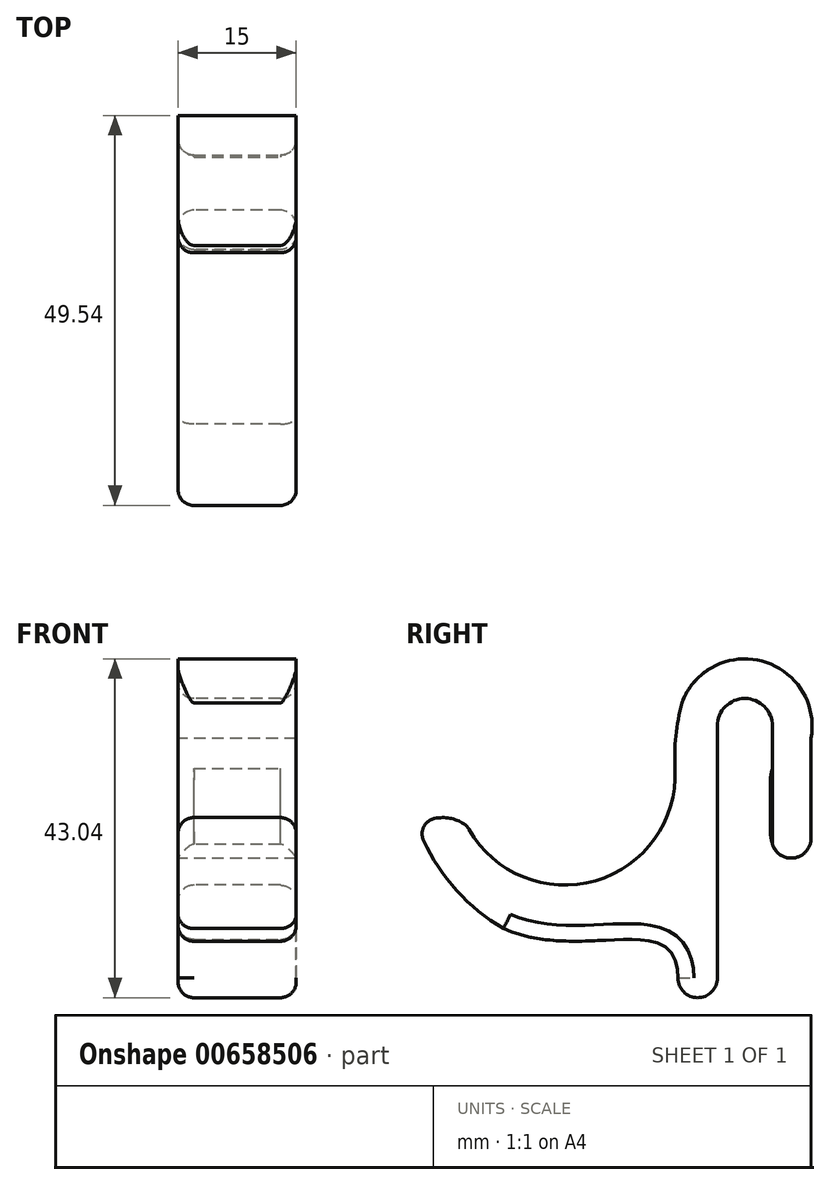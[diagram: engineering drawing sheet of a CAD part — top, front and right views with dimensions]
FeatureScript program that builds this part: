
annotation { "Feature Type Name" : "Feature", "Feature Type Description" : "" }
export const myFeature = defineFeature(function(context is Context, id is Id, definition is map)
    precondition{}
    {
        {
            var Q0;
            Q0=qCreatedBy(makeId("Right.planeOp"),FACE);
            var sketch = newSketch(context, id + "F0", { "sketchPlane" : qUnion([Q0])});
            skLineSegment(sketch, "E0.left", {"start": v(0, 0) * mm, "end": v(0, 32) * mm});
            skLineSegment(sketch, "E0.right", {"start": v(7, 17) * mm, "end": v(7, 32) * mm});
            skArc(sketch, "E1", {"start": v(7, 32) * mm, "mid": v(3.5, 35.5) * mm, "end": v(0, 32) * mm});
            skLineSegment(sketch, "E2.0", {"start": v(11.9, 17.72) * mm, "end": v(11.9, 30.43) * mm});
            skArc(sketch, "E2.1", {"start": v(11.9, 30.43) * mm, "mid": v(5.77, 40.23) * mm, "end": v(-4.5, 34.97) * mm});
            skArc(sketch, "E3", {"start": v(7, 17) * mm, "mid": v(9.76, 15.25) * mm, "end": v(11.9, 17.72) * mm});
            skArc(sketch, "E4", {"start": v(-5, 0) * mm, "mid": v(-2.5, -2.5) * mm, "end": v(0, 0) * mm});
            skLineSegment(sketch, "E5", {"start": v(-4.5, 34.97) * mm, "end": v(-6, 29.97) * mm});
            skArc(sketch, "E6", {"start": v(-31.74, 19.25) * mm, "mid": v(-13.98, 12.87) * mm, "end": v(-6, 29.97) * mm});
            skArc(sketch, "E7", {"start": v(-31.74, 19.25) * mm, "mid": v(-34.9, 20.37) * mm, "end": v(-38.06, 19.25) * mm});
            skArc(sketch, "E8", {"start": v(-38.06, 19.25) * mm, "mid": v(-33.74, 11.83) * mm, "end": v(-27.18, 6.28) * mm});
            skFitSpline(sketch, "E9", {"points": [v(-27.18, 6.28) * mm, v(-5, 0) * mm], "startDerivative": vector(30.25, -13.4) * mm, "endDerivative": vector(-0.02, -27.31) * mm});
            skSolve(sketch);
        }
        {
            var Q0;
            Q0=makeQuery(id+"F0.imprint","IMPRINT",FACE,{"disambiguationData":[TD([[makeQuery(id+"F0.imprint","IMPRINT",EDGE,{"derivedFrom":sQuery(id+"F0.wireOp",EDGE,"E0.left")}),1.0]])]});
            extrude(context, id + "F1", {"entities" : qUnion([Q0]), "depth" : 15 * mm, "offsetDistance" : 25 * mm});
        }
        {
            var Q0;
            Q0=makeQuery(id+"F1.opExtrude","SWEPT_EDGE",EDGE,{"disambiguationData":[OSD([sQuery(id+"F0.wireOp",EDGE,"E5"),sQuery(id+"F0.wireOp",EDGE,"E6")])]});
            fillet(context, id + "F2", {"entities" : qUnion([Q0]), "radius" : 28.53 * mm, "tangentPropagation" : true, "allowEdgeOverflow" : false});
        }
        {
            var Q0;
            Q0=makeQuery(id+"F1.opExtrude","SWEPT_EDGE",EDGE,{"disambiguationData":[OSD([sQuery(id+"F0.wireOp",EDGE,"E6"),sQuery(id+"F0.wireOp",EDGE,"E7")])]});
            var Q1;
            Q1=makeQuery(id+"F1.opExtrude","SWEPT_EDGE",EDGE,{"disambiguationData":[OSD([sQuery(id+"F0.wireOp",EDGE,"E7"),sQuery(id+"F0.wireOp",EDGE,"E8")])]});
            fillet(context, id + "F3", {"entities" : qUnion([Q0, Q1]), "radius" : 2 * mm, "tangentPropagation" : true, "allowEdgeOverflow" : false});
        }
        {
            var Q0;
            Q0=makeQuery(id+"F1.opExtrude","CAP_EDGE",EDGE,{"disambiguationData":[OSD([sQuery(id+"F0.wireOp",EDGE,"E6")])],"isStart":true});
            var Q1;
            Q1=makeQuery(id+"F1.opExtrude","CAP_EDGE",EDGE,{"disambiguationData":[OSD([sQuery(id+"F0.wireOp",EDGE,"E9")])],"isStart":true});
            var Q2;
            Q2=makeQuery(id+"F1.opExtrude","CAP_EDGE",EDGE,{"disambiguationData":[OSD([sQuery(id+"F0.wireOp",EDGE,"E8")])],"isStart":true});
            var Q3;
            Q3=makeQuery(id+"F1.opExtrude","CAP_EDGE",EDGE,{"disambiguationData":[OSD([sQuery(id+"F0.wireOp",EDGE,"E6")])],"isStart":false});
            var Q4;
            Q4=makeQuery(id+"F1.opExtrude","CAP_EDGE",EDGE,{"disambiguationData":[OSD([sQuery(id+"F0.wireOp",EDGE,"E9")])],"isStart":false});
            var Q5;
            Q5=makeQuery(id+"F1.opExtrude","CAP_EDGE",EDGE,{"disambiguationData":[OSD([sQuery(id+"F0.wireOp",EDGE,"E8")])],"isStart":false});
            fillet(context, id + "F4", {"entities" : qUnion([Q0, Q1, Q2, Q3, Q4, Q5]), "radius" : 2 * mm, "tangentPropagation" : true, "allowEdgeOverflow" : false});
        }
        {
            var Q0;
            Q0=makeQuery(id+"F1.opExtrude","SWEPT_FACE",FACE,{"disambiguationData":[OSD([sQuery(id+"F0.wireOp",EDGE,"E0.right")])]});
            var sketch = newSketch(context, id + "F5", { "sketchPlane" : qUnion([Q0])});
            skLineSegment(sketch, "E10", {"start": v(2, 26.64) * mm, "end": v(13, 26.64) * mm});
            skSolve(sketch);
        }
        {
            var Q0;
            {var subQ0=sQuery(id+"F5.wireOp",EDGE,"E10");Q0=makeQuery(id+"F5.imprint","IMPRINT",FACE,{"disambiguationData":[TD([[makeQuery(id+"F5.imprint","IMPRINT",EDGE,{"derivedFrom":subQ0}),-1.0]])]});}
            extrude(context, id + "F6", {"entities" : qUnion([Q0]), "operationType" : NewBodyOperationType.ADD, "depth" : .25 * mm, "offsetDistance" : 25 * mm});
        }
        {
            var Q0;
            Q0=makeQuery(id+"F6.opExtrude","CAP_EDGE",EDGE,{"disambiguationData":[OSD([sQuery(id+"F5.wireOp",EDGE,"E10")])],"isStart":false});
            var Q1;
            Q1=makeQuery(id+"F6.opExtrude","CAP_EDGE",EDGE,{"disambiguationData":[OSD([sQuery(id+"F0.wireOp",EDGE,"E0.right"),sQuery(id+"F0.wireOp",EDGE,"E3")])],"isStart":false});
            fillet(context, id + "F7", {"entities" : qUnion([Q0, Q1]), "radius" : 5 * mm, "tangentPropagation" : true, "allowEdgeOverflow" : false});
        }
    });
